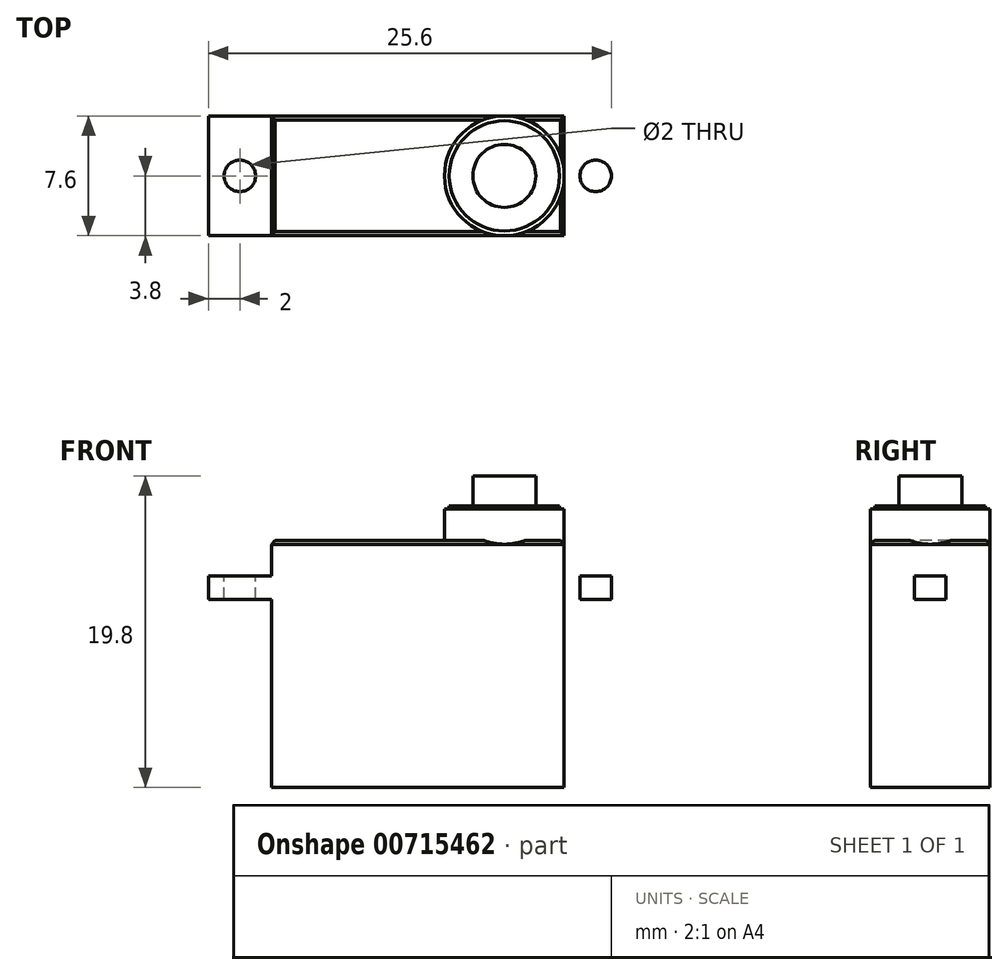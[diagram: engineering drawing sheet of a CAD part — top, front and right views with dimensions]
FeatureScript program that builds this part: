
annotation { "Feature Type Name" : "Feature", "Feature Type Description" : "" }
export const myFeature = defineFeature(function(context is Context, id is Id, definition is map)
    precondition{}
    {
        {
            var Q0;
            Q0=qCreatedBy(makeId("Front.planeOp"),FACE);
            var sketch = newSketch(context, id + "F0", { "sketchPlane" : qUnion([Q0])});
            skLineSegment(sketch, "E0.bottom", {"start": v(-9.3, 15.7) * mm, "end": v(9.3, 15.7) * mm});
            skLineSegment(sketch, "E0.top", {"start": v(-9.3, 0) * mm, "end": v(9.3, 0) * mm});
            skLineSegment(sketch, "E0.left", {"start": v(-9.3, 15.7) * mm, "end": v(-9.3, 13.45) * mm});
            skLineSegment(sketch, "E0.right", {"start": v(9.3, 15.7) * mm, "end": v(9.3, 13.45) * mm});
            skLineSegment(sketch, "E1.bottom", {"start": v(9.28, 11.95) * mm, "end": v(13.3, 11.95) * mm});
            skLineSegment(sketch, "E1.top", {"start": v(9.28, 13.45) * mm, "end": v(13.3, 13.45) * mm});
            skLineSegment(sketch, "E1.right", {"start": v(13.3, 11.95) * mm, "end": v(13.3, 13.45) * mm});
            skLineSegment(sketch, "E2.trimOffspring", {"start": v(9.3, 11.95) * mm, "end": v(9.3, 0) * mm});
            skLineSegment(sketch, "E3.MirrorCS", {"start": v(-9.28, 11.95) * mm, "end": v(-13.3, 11.95) * mm});
            skLineSegment(sketch, "E4.MirrorCS", {"start": v(-9.28, 13.45) * mm, "end": v(-13.3, 13.45) * mm});
            skLineSegment(sketch, "E5.MirrorCS", {"start": v(-13.3, 11.95) * mm, "end": v(-13.3, 13.45) * mm});
            skLineSegment(sketch, "E6.trimOffspring", {"start": v(-9.3, 11.95) * mm, "end": v(-9.3, 0) * mm});
            skSolve(sketch);
        }
        {
            var Q0;
            Q0 = qSketchRegion(id + "F0", true);
            extrude(context, id + "F1", {"entities" : qUnion([Q0]), "depth" : 7.6 * mm, "offsetDistance" : 25 * mm});
        }
        {
            var Q0;
            Q0=makeQuery(id+"F1.opExtrude","SWEPT_FACE",FACE,{"disambiguationData":[OSD([sQuery(id+"F0.wireOp",EDGE,"E4.MirrorCS")])]});
            var sketch = newSketch(context, id + "F2", { "sketchPlane" : qUnion([Q0])});
            skLineSegment(sketch, "E7.0.0", {"start": v(9.3, 0) * mm, "end": v(-9.3, 0) * mm});
            skLineSegment(sketch, "E7.0.1", {"start": v(-9.3, 0) * mm, "end": v(-9.3, -7.6) * mm});
            skLineSegment(sketch, "E7.0.2", {"start": v(-9.3, -7.6) * mm, "end": v(9.3, -7.6) * mm});
            skLineSegment(sketch, "E7.0.3", {"start": v(9.3, -7.6) * mm, "end": v(9.3, 0) * mm});
            skLineSegment(sketch, "E8.0.0", {"start": v(13.3, 0) * mm, "end": v(9.3, 0) * mm});
            skLineSegment(sketch, "E8.0.1", {"start": v(9.3, 0) * mm, "end": v(9.3, -7.6) * mm});
            skLineSegment(sketch, "E8.0.2", {"start": v(9.3, -7.6) * mm, "end": v(13.3, -7.6) * mm});
            skLineSegment(sketch, "E8.0.3", {"start": v(13.3, -7.6) * mm, "end": v(13.3, 0) * mm});
            skLineSegment(sketch, "E9.0.0", {"start": v(-9.3, 0) * mm, "end": v(-13.3, 0) * mm});
            skLineSegment(sketch, "E9.0.1", {"start": v(-13.3, 0) * mm, "end": v(-13.3, -7.6) * mm});
            skLineSegment(sketch, "E9.0.2", {"start": v(-13.3, -7.6) * mm, "end": v(-9.3, -7.6) * mm});
            skLineSegment(sketch, "E9.0.3", {"start": v(-9.3, -7.6) * mm, "end": v(-9.3, 0) * mm});
            skLineSegment(sketch, "E10", {"start": v(0, 0) * mm, "end": v(0, -7.6) * mm, "construction": true});
            skLineSegment(sketch, "E11", {"start": v(-11.3, 0) * mm, "end": v(-11.3, -7.6) * mm, "construction": true});
            skLineSegment(sketch, "E12", {"start": v(-13.3, -3.8) * mm, "end": v(-9.3, -3.8) * mm, "construction": true});
            skCircle(sketch, "E13", {"center": v(-11.3, -3.8) * mm, "radius": 1 * mm});
            skCircle(sketch, "E14.MirrorC", {"center": v(11.3, -3.8) * mm, "radius": 1 * mm});
            skSolve(sketch);
        }
        {
            var Q0;
            Q0=makeQuery(id+"F2.imprint","IMPRINT",FACE,{"disambiguationData":[TD([[makeQuery(id+"F2.imprint","IMPRINT",EDGE,{"derivedFrom":sQuery(id+"F2.wireOp",EDGE,"E13")}),1.0]])]});
            var Q1;
            Q1=makeQuery(id+"F2.imprint","IMPRINT",FACE,{"disambiguationData":[TD([[makeQuery(id+"F2.imprint","IMPRINT",EDGE,{"derivedFrom":sQuery(id+"F2.wireOp",EDGE,"E14.MirrorC")}),-1.0]])]});
            extrude(context, id + "F3", {"entities" : qUnion([Q0, Q1]), "operationType" : NewBodyOperationType.REMOVE, "endBound" : BoundingType.THROUGH_ALL, "oppositeDirection" : true, "depth" : 25 * mm, "offsetDistance" : 25 * mm});
        }
        {
            var Q0;
            Q0=makeQuery(id+"F1.opExtrude","SWEPT_FACE",FACE,{"disambiguationData":[OSD([sQuery(id+"F0.wireOp",EDGE,"E0.bottom")])]});
            var sketch = newSketch(context, id + "F4", { "sketchPlane" : qUnion([Q0])});
            skLineSegment(sketch, "E15", {"start": v(-9.3, -3.8) * mm, "end": v(9.3, -3.8) * mm, "construction": true});
            skCircle(sketch, "E16", {"center": v(5.5, -3.8) * mm, "radius": 3.8 * mm});
            skCircle(sketch, "E17", {"center": v(5.5, -3.8) * mm, "radius": 2 * mm});
            skCircle(sketch, "E18", {"center": v(5.5, -3.8) * mm, "radius": 3.5 * mm});
            skSolve(sketch);
        }
        {
            var Q0;
            Q0 = qSketchRegion(id + "F4", true);
            var Q1;
            Q1=makeQuery(id+"F4.imprint","IMPRINT",FACE,{"disambiguationData":[TD([[makeQuery(id+"F4.imprint","IMPRINT",EDGE,{"derivedFrom":sQuery(id+"F4.wireOp",EDGE,"E17")}),1.0]])]});
            var Q2;
            Q2=makeQuery(id+"F4.imprint","IMPRINT",FACE,{"disambiguationData":[TD([[makeQuery(id+"F4.imprint","IMPRINT",EDGE,{"derivedFrom":sQuery(id+"F4.wireOp",EDGE,"E17")}),-1.0]])]});
            extrude(context, id + "F5", {"entities" : qUnion([Q0, Q1, Q2]), "operationType" : NewBodyOperationType.ADD, "depth" : 2 * mm, "offsetDistance" : 25 * mm});
        }
        {
            var Q0;
            Q0=makeQuery(id+"F4.imprint","IMPRINT",FACE,{"disambiguationData":[TD([[makeQuery(id+"F4.imprint","IMPRINT",EDGE,{"derivedFrom":sQuery(id+"F4.wireOp",EDGE,"E17")}),-1.0]])]});
            var Q1;
            Q1=makeQuery(id+"F4.imprint","IMPRINT",FACE,{"disambiguationData":[TD([[makeQuery(id+"F4.imprint","IMPRINT",EDGE,{"derivedFrom":sQuery(id+"F4.wireOp",EDGE,"E17")}),1.0]])]});
            var Q2;
            Q2=makeQuery(id+"F5.opExtrude","CAP_FACE",FACE,{"disambiguationData":[OSD([sQuery(id+"F4.wireOp",EDGE,"E16")])],"isStart":false});
            var Q3;
            Q3=makeQuery(id+"F5.opExtrude","CAP_FACE",FACE,{"disambiguationData":[OSD([sQuery(id+"F4.wireOp",EDGE,"E16")])],"isStart":false});
            extrude(context, id + "F6", {"entities" : qUnion([Q0, Q1]), "operationType" : NewBodyOperationType.ADD, "depth" : 2.17 * mm, "endBoundEntityFace" : qUnion([Q2]), "offsetDistance" : 25 * mm});
        }
        {
            var Q0;
            Q0=makeQuery(id+"F4.imprint","IMPRINT",FACE,{"disambiguationData":[TD([[makeQuery(id+"F4.imprint","IMPRINT",EDGE,{"derivedFrom":sQuery(id+"F4.wireOp",EDGE,"E17")}),1.0]])]});
            extrude(context, id + "F7", {"entities" : qUnion([Q0]), "operationType" : NewBodyOperationType.ADD, "depth" : 4.1 * mm, "offsetDistance" : 25 * mm});
        }
        {
            var Q0;
            {var subQ0=sQuery(id+"F0.wireOp",EDGE,"E0.bottom");var subQ1=sQuery(id+"F0.wireOp",EDGE,"E0.left");Q0=makeQuery(id+"F5.boolean.opBoolean","SPLIT",EDGE,{"disambiguationData":[TD([makeQuery(id+"F1.opExtrude","SWEPT_FACE",FACE,{"disambiguationData":[OSD([subQ1])]})])],"derivedFrom":makeQuery(id+"F1.opExtrude","CAP_EDGE",EDGE,{"disambiguationData":[OSD([subQ0])],"isStart":false})});}
            var Q1;
            Q1=makeQuery(id+"F1.opExtrude","SWEPT_EDGE",EDGE,{"disambiguationData":[OSD([sQuery(id+"F0.wireOp",EDGE,"E0.bottom"),sQuery(id+"F0.wireOp",EDGE,"E0.left")])]});
            var Q2;
            {var subQ0=sQuery(id+"F0.wireOp",EDGE,"E0.bottom");var subQ1=sQuery(id+"F0.wireOp",EDGE,"E0.left");Q2=makeQuery(id+"F5.boolean.opBoolean","SPLIT",EDGE,{"disambiguationData":[TD([makeQuery(id+"F1.opExtrude","SWEPT_FACE",FACE,{"disambiguationData":[OSD([subQ1])]})])],"derivedFrom":makeQuery(id+"F1.opExtrude","CAP_EDGE",EDGE,{"disambiguationData":[OSD([subQ0])],"isStart":true})});}
            var Q3;
            {var subQ0=sQuery(id+"F0.wireOp",EDGE,"E0.bottom");var subQ1=sQuery(id+"F0.wireOp",EDGE,"E0.right");Q3=makeQuery(id+"F5.boolean.opBoolean","SPLIT",EDGE,{"disambiguationData":[TD([makeQuery(id+"F1.opExtrude","CAP_FACE",FACE,{"disambiguationData":[OSD([subQ0,sQuery(id+"F0.wireOp",EDGE,"E0.top"),sQuery(id+"F0.wireOp",EDGE,"E0.left"),subQ1,sQuery(id+"F0.wireOp",EDGE,"E1.bottom"),sQuery(id+"F0.wireOp",EDGE,"E1.top"),sQuery(id+"F0.wireOp",EDGE,"E1.right"),sQuery(id+"F0.wireOp",EDGE,"E2.trimOffspring"),sQuery(id+"F0.wireOp",EDGE,"E3.MirrorCS"),sQuery(id+"F0.wireOp",EDGE,"E4.MirrorCS"),sQuery(id+"F0.wireOp",EDGE,"E5.MirrorCS"),sQuery(id+"F0.wireOp",EDGE,"E6.trimOffspring")])],"isStart":false})])],"derivedFrom":makeQuery(id+"F1.opExtrude","SWEPT_EDGE",EDGE,{"disambiguationData":[OSD([subQ0,subQ1])]})});}
            chamfer(context, id + "F8", {"entities" : qUnion([Q0, Q1, Q2, Q3]), "width" : .25 * mm, "tangentPropagation" : true});
        }
    });
